# Revit family: QF_COMENDA_6C1133_6C1142_AG_CAT
name_source: partatom
category: Attrezzature speciali
units: mm (PartAtom-declared; Revit-internal decimal feet)

## family parameters
Basato su piano di lavoro = No
Condiviso = No
Numero OmniClass = 23.40.40.14
Punto di calcolo locali = No
Quota connettore circolare = Usa diametro
Sempre verticale = Sì
Taglio con vuoti quando caricato = No
Tipo di parte = Normale
Titolo OmniClass = Food Service Equipment

## types (2) — shared parameters
Altezza = 1900 mm  [stored 6.2336 ft]
Altezza allacciamento elettrico da pavimento finito = 214 mm  [stored 0.7021 ft]
Altezza da terra raccordo acqua calda = 208 mm
Altezza dello scarico diretto acqua da pavimento finito = 214 mm  [stored 0.7021 ft]
Diametro dello scarico diretto di acqua = 1 1/2"
Diametro raccordo acqua calda = 1"
Fase = 3
Frequenza = 50 Hz
Lunghezza = 625 mm  [stored 2.05052 ft]
Numero dei poli = 3
Peso netto = 125.00 kg
Pressione minima acqua calda = 2000.0 Pa
Produttore = COMENDA
Profondità = 740 mm  [stored 2.42782 ft]
Protezione contro le sovracorrenti = 20 A
Temperatura raccomandata per acqua calda = 50 °C
Tensione = 400 V
URL = www.comenda.fr
URL catalogo = https://comenda.fr
zero-valued in all types: Prospetto di default

## per-type parameters (varying)
| type | Corrente di funzionamento normale | Descrizione | Modello | Potenza elettrica |
| 6C1142_GA | 16 A | MULTIPOWER HOOD SINGLE DISH DISHWASHER WHIT CRC | Ci 16 R CRC | 13000 W |
| 6C1133_GA | 15 A | MULTIPOWER HOOD SINGLE DISH DISHWASHER WITH CRC | Ci 10 R CRC | 10600 W |

note: [stored X ft] marks values corroborated as IEEE doubles in the binary element streams (Revit-internal decimal feet)

## geometry (parser evidence)
native form markers: Sweep x2
no freeform markers — native parametric forms only
